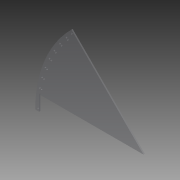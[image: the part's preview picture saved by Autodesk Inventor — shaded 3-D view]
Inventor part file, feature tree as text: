
AUTODESK INVENTOR PART (.ipt)
format: ipt  version: 2013 (Build 170138000, 138)  size: 107,008 bytes
history: native  units: in
note: dims shown in document units (in); Inventor stores cm internally (conversion verified against a paired STEP export)
features: extrude x2, sketch x2, reference x2
ambient origin geometry x8: Origin, YZ Plane, XZ Plane, XY Plane, X Axis, Y Axis, Z Axis, Center Point
feature tree (6):
  extrude  "Extrusion3"  Depth=0.375in
  extrude  "Extrusion5"  Depth=0.125in TaperAngle=0.0deg
  sketch  "Sketch3"  dims[d10=1.5in d12=0.375in]
  sketch  "Sketch4"  dims[d14=0.125in d15=0.0in d19=0.125in d20=0.0in]
  reference  "Reference1"
  reference  "Reference2"
